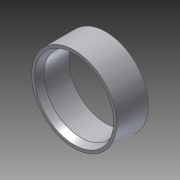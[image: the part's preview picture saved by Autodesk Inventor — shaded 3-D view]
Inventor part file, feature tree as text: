
AUTODESK INVENTOR PART (.ipt)
format: ipt  version: 2014 SP1 (Build 180222100, 222)  size: 97,280 bytes
history: native  units: in
note: dims shown in document units (in); Inventor stores cm internally (conversion verified against a paired STEP export)
features: chamfer x1, other x1, imported_body x1
ambient origin geometry x8: Origin, YZ Plane, XZ Plane, XY Plane, X Axis, Y Axis, Z Axis, Center Point
bodies: Body1 (feature_tree)
feature tree (3):
  chamfer  "Chamfer1"  [1 undecoded]
  other  "worm gear ring.ipt1"
  imported_body  "Base1"
note: 1 required parameter value undecoded (feature->parameter linkage not recoverable at this tier; creation-order binding heuristic only, values carry confidence <= 0.55)
